# Revit family: PM8SUB-B
name_source: partatom
category: Communication Devices
revit_build: Autodesk Revit 2014 (Build: 20140709_2115(x64)
units: mm (PartAtom-declared; Revit-internal decimal feet)

## types (1)
- Pendant Mount Loudspeaker
    100V Taps = 7.5, 15, 30, 60W &amp; 8Ω
    70V Taps = 7.5, 15, 30, 60W &amp; 8Ω
    Baffle Material = <By Category>
    Body Material = <By Category>
    Color = <By Category>
    Cost = 359.99 $
    Cost MSRP = 359.99 $
    Coverage Horizontal = 110.00°
    Coverage Vertical = 110.00°
    Description = 8" PENDANT MOUNT SUBWOOFER WITH 60-WATT 70.7V TRANSFORMER - BLACK
    Dispersion Angle = 90.00°
    Enclosure Material = <By Category>
    Family Code (default) = LOUD SPEAKERS
    Frequency Response  = 46Hz - 160Hz
    Grill Material = <By Category>
    HF Driver = Coaxially Mounted Titanium Compression Driver
    Height = 16.62 "
    Horizontal Symmetry = Yes
    IQ Category = SPEAKERS
    Impedance = 8
    Ingress Protection = IP-21
    Manufacturer = ATLAS SOUND
    Manufacturer URL = https://www.atlasied.com
    Market = Commercial, Higher Education, Emergency
    MasterFormat = 27 41 13
    MaterFormat Title = SPEAKERS
    Model = PM8SUB-B
    Mount Material = QF_Plastic - Black - Matte
    OmniClass Number = 23-37 17 13 19
    OmniClass Title = SPEAKERS
    Power Rating (RMS) = 150 Watts
    Product Page URL = https://www.atlasied.com
    SPL Max = 107
    ScheduleType |RF| = AtlasIED Master
    Sensitivity = 92
    Speaker Dispersion = 120.00°
    Speaker Type = S1
    Transformer Option = Yes
    URL = www.atlassound.com
    Vertical Symmetry = Yes
    Warranty = 5 Year
    Weight Product = 21
    Width = 12.28 "

## geometry (parser evidence)
native form markers: Blend x10, Sweep x2
no freeform markers — native parametric forms only
